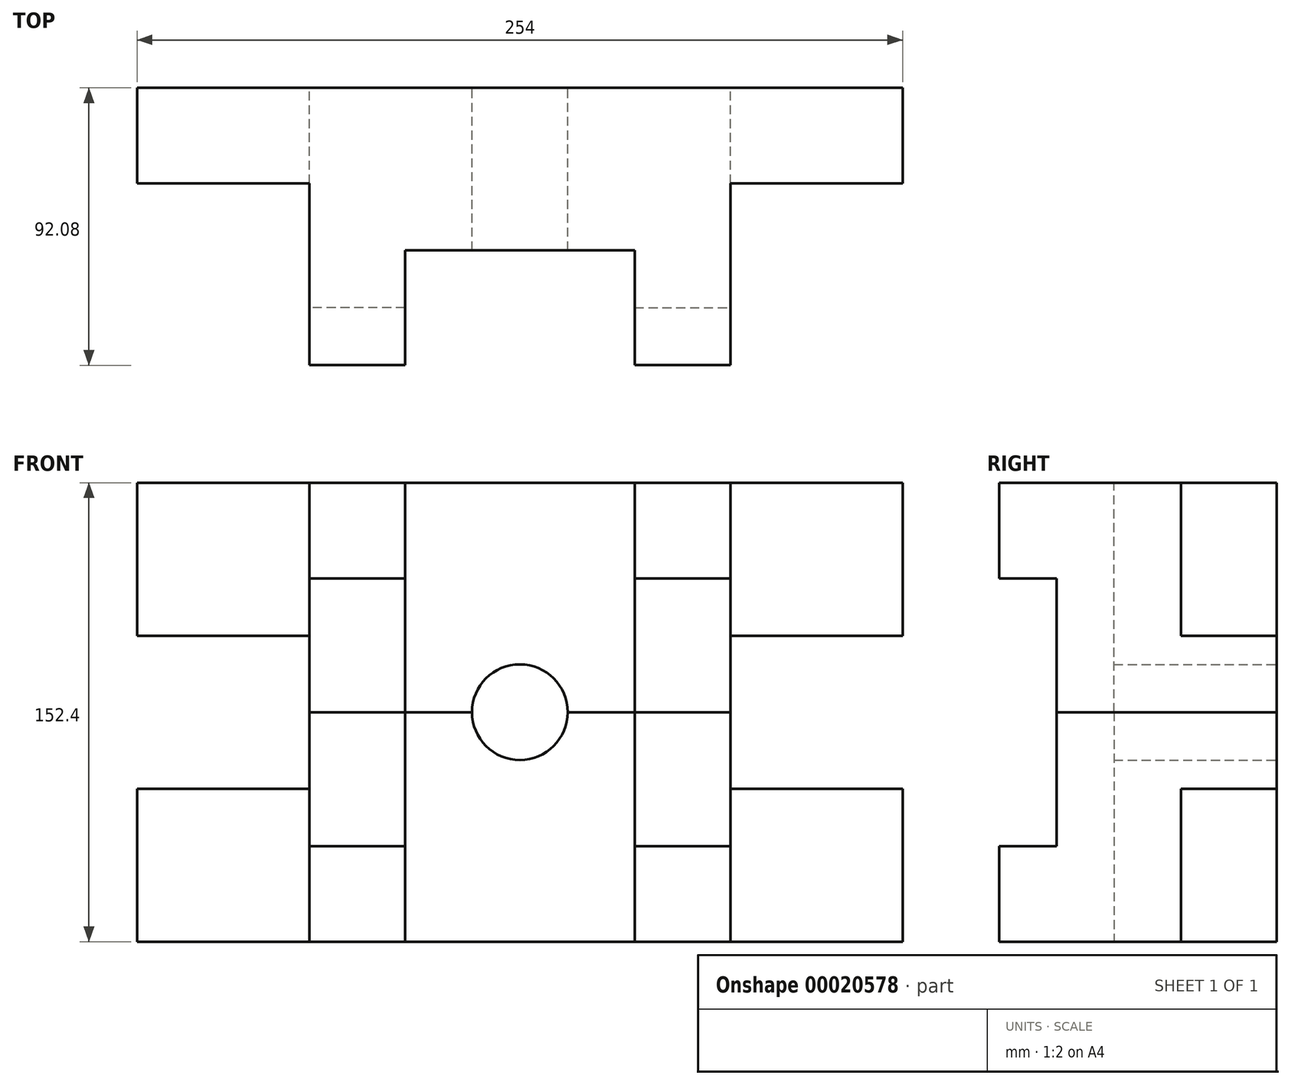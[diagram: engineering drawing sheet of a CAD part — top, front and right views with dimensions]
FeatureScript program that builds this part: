
annotation { "Feature Type Name" : "Feature", "Feature Type Description" : "" }
export const myFeature = defineFeature(function(context is Context, id is Id, definition is map)
    precondition{}
    {
        {
            var Q0;
            Q0=qCreatedBy(makeId("Front.planeOp"),FACE);
            var sketch = newSketch(context, id + "F0", { "sketchPlane" : qUnion([Q0])});
            skLineSegment(sketch, "E0.bottom", {"start": v(0, 0) * mm, "end": v(127, 0) * mm});
            skLineSegment(sketch, "E0.top", {"start": v(0, 76.2) * mm, "end": v(127, 76.2) * mm});
            skLineSegment(sketch, "E0.left", {"start": v(0, 0) * mm, "end": v(0, 76.2) * mm});
            skLineSegment(sketch, "E0.right", {"start": v(127, 0) * mm, "end": v(127, 76.2) * mm});
            skLineSegment(sketch, "E1", {"start": v(69.85, 76.2) * mm, "end": v(69.85, 0) * mm});
            skLineSegment(sketch, "E2", {"start": v(38.1, 76.2) * mm, "end": v(38.1, 0) * mm});
            skPoint(sketch, "E3", {"position": v(38.1, 31.75) * mm});
            skPoint(sketch, "E4", {"position": v(69.85, 31.75) * mm});
            skPoint(sketch, "E5", {"position": v(38.1, 59.6) * mm});
            skPoint(sketch, "E6", {"position": v(69.85, 50.8) * mm});
            skLineSegment(sketch, "E7", {"start": v(38.1, 31.75) * mm, "end": v(69.85, 31.75) * mm});
            skArc(sketch, "E8", {"start": v(0, 60.33) * mm, "mid": v(11.23, 64.97) * mm, "end": v(15.87, 76.2) * mm});
            skPoint(sketch, "E9", {"position": v(127, 50.8) * mm});
            skLineSegment(sketch, "E10", {"start": v(69.85, 50.8) * mm, "end": v(127, 50.8) * mm});
            skSolve(sketch);
        }
        {
            var Q0;
            {var subQ0=sQuery(id+"F0.wireOp",EDGE,"E10");Q0=makeQuery(id+"F0.imprint","IMPRINT",FACE,{"disambiguationData":[TD([[makeQuery(id+"F0.imprint","IMPRINT",EDGE,{"derivedFrom":subQ0}),-1.0]])]});}
            extrude(context, id + "F1", {"entities" : qUnion([Q0]), "depth" : 31.75 * mm});
        }
        {
            var Q0;
            {var subQ0=sQuery(id+"F0.wireOp",EDGE,"E8");Q0=makeQuery(id+"F0.imprint","IMPRINT",FACE,{"disambiguationData":[TD([[makeQuery(id+"F0.imprint","IMPRINT",EDGE,{"derivedFrom":subQ0}),-1.0]])]});}
            extrude(context, id + "F2", {"entities" : qUnion([Q0]), "depth" : 53.97 * mm});
        }
        {
            var Q0;
            {var subQ0=sQuery(id+"F0.wireOp",EDGE,"E7");Q0=makeQuery(id+"F0.imprint","IMPRINT",FACE,{"disambiguationData":[TD([[makeQuery(id+"F0.imprint","IMPRINT",EDGE,{"derivedFrom":subQ0}),-1.0]])]});}
            extrude(context, id + "F3", {"entities" : qUnion([Q0]), "depth" : 92.07 * mm});
        }
        {
            var Q0;
            {var subQ0=sQuery(id+"F0.wireOp",EDGE,"E7");Q0=makeQuery(id+"F0.imprint","IMPRINT",FACE,{"disambiguationData":[TD([[makeQuery(id+"F0.imprint","IMPRINT",EDGE,{"derivedFrom":subQ0}),1.0]])]});}
            extrude(context, id + "F4", {"entities" : qUnion([Q0]), "depth" : 73.02 * mm});
        }
        {
            var Q0;
            Q0=makeQuery(id+"F1.opExtrude","SWEPT_BODY",BODY,{"disambiguationData":[OSD([sQuery(id+"F0.wireOp",EDGE,"E0.bottom"),sQuery(id+"F0.wireOp",EDGE,"E0.right"),sQuery(id+"F0.wireOp",EDGE,"E1"),sQuery(id+"F0.wireOp",EDGE,"E10")])]});
            var Q1;
            Q1=makeQuery(id+"F2.opExtrude","SWEPT_BODY",BODY,{"disambiguationData":[OSD([sQuery(id+"F0.wireOp",EDGE,"E0.bottom"),sQuery(id+"F0.wireOp",EDGE,"E0.top"),sQuery(id+"F0.wireOp",EDGE,"E2"),sQuery(id+"F0.wireOp",EDGE,"E0.left"),sQuery(id+"F0.wireOp",EDGE,"E8")])]});
            var Q2;
            Q2=makeQuery(id+"F3.opExtrude","SWEPT_BODY",BODY,{"disambiguationData":[OSD([sQuery(id+"F0.wireOp",EDGE,"E0.bottom"),sQuery(id+"F0.wireOp",EDGE,"E1"),sQuery(id+"F0.wireOp",EDGE,"E2"),sQuery(id+"F0.wireOp",EDGE,"E7")])]});
            var Q3;
            Q3=makeQuery(id+"F4.opExtrude","SWEPT_BODY",BODY,{"disambiguationData":[OSD([sQuery(id+"F0.wireOp",EDGE,"E0.top"),sQuery(id+"F0.wireOp",EDGE,"E1"),sQuery(id+"F0.wireOp",EDGE,"E2"),sQuery(id+"F0.wireOp",EDGE,"E7")])]});
            var Q4;
            Q4=makeQuery(id+"F2.opExtrude","SWEPT_FACE",FACE,{"disambiguationData":[OSD([sQuery(id+"F0.wireOp",EDGE,"E0.left")])]});
            mirror(context, id + "F5", {"operationType" : NewBodyOperationType.ADD, "entities" : qUnion([Q0, Q1, Q2, Q3]), "mirrorPlane" : qUnion([Q4])});
        }
        {
            var Q0;
            Q0=makeQuery(id+"F3.opExtrude","SWEPT_BODY",BODY,{"disambiguationData":[OSD([sQuery(id+"F0.wireOp",EDGE,"E0.bottom"),sQuery(id+"F0.wireOp",EDGE,"E1"),sQuery(id+"F0.wireOp",EDGE,"E2"),sQuery(id+"F0.wireOp",EDGE,"E7")])]});
            var Q1;
            Q1=makeQuery(id+"F1.opExtrude","SWEPT_BODY",BODY,{"disambiguationData":[OSD([sQuery(id+"F0.wireOp",EDGE,"E0.bottom"),sQuery(id+"F0.wireOp",EDGE,"E0.right"),sQuery(id+"F0.wireOp",EDGE,"E1"),sQuery(id+"F0.wireOp",EDGE,"E10")])]});
            var Q2;
            Q2=makeQuery(id+"F4.opExtrude","SWEPT_BODY",BODY,{"disambiguationData":[OSD([sQuery(id+"F0.wireOp",EDGE,"E0.top"),sQuery(id+"F0.wireOp",EDGE,"E1"),sQuery(id+"F0.wireOp",EDGE,"E2"),sQuery(id+"F0.wireOp",EDGE,"E7")])]});
            var Q3;
            Q3=makeQuery(id+"F2.opExtrude","SWEPT_BODY",BODY,{"disambiguationData":[OSD([sQuery(id+"F0.wireOp",EDGE,"E0.bottom"),sQuery(id+"F0.wireOp",EDGE,"E0.top"),sQuery(id+"F0.wireOp",EDGE,"E2"),sQuery(id+"F0.wireOp",EDGE,"E0.left"),sQuery(id+"F0.wireOp",EDGE,"E8")])]});
            var Q4;
            {var subQ0=sQuery(id+"F0.wireOp",EDGE,"E0.top");Q4=makeQuery(id+"F5.boolean.opBoolean","MERGE",FACE,{"derivedFrom":[makeQuery(id+"F5.opPattern","COPY",FACE,{"derivedFrom":makeQuery(id+"F2.opExtrude","SWEPT_FACE",FACE,{"disambiguationData":[OSD([subQ0])]}),"instanceName":"1"}),makeQuery(id+"F5.opPattern","COPY",FACE,{"derivedFrom":makeQuery(id+"F4.opExtrude","SWEPT_FACE",FACE,{"disambiguationData":[OSD([subQ0])]}),"instanceName":"1"})]});}
            mirror(context, id + "F6", {"entities" : qUnion([Q0, Q1, Q2, Q3]), "mirrorPlane" : qUnion([Q4])});
        }
    });
